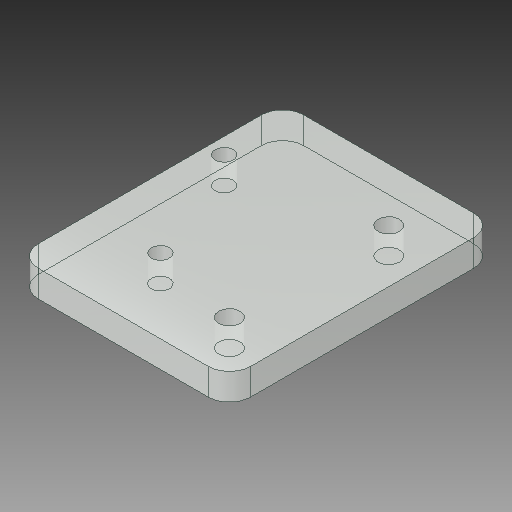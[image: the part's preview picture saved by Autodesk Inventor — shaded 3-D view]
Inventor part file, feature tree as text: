
AUTODESK INVENTOR PART (.ipt)
format: ipt  version: 2019 (Build 230136000, 136)  size: 128,000 bytes
history: native  units: mm
features: extrude x1, fillet x1, sketch x1
ambient origin geometry x8: Origin, YZ Plane, XZ Plane, XY Plane, X Axis, Y Axis, Z Axis, Center Point
bodies: Body1 (feature_tree)
feature tree (3):
  extrude  "Extrusion2"  Depth=50.0mm
  fillet  "Fillet2"  Radius=10.0mm
  sketch  "Sketch1"  dims[d0=40.0mm d1=50.0mm d5=10.0mm d6=4.0mm d7=4.0mm d8=10.0mm d9=10.0mm d10=5.0mm d11=0.0mm d12=4.0mm]
